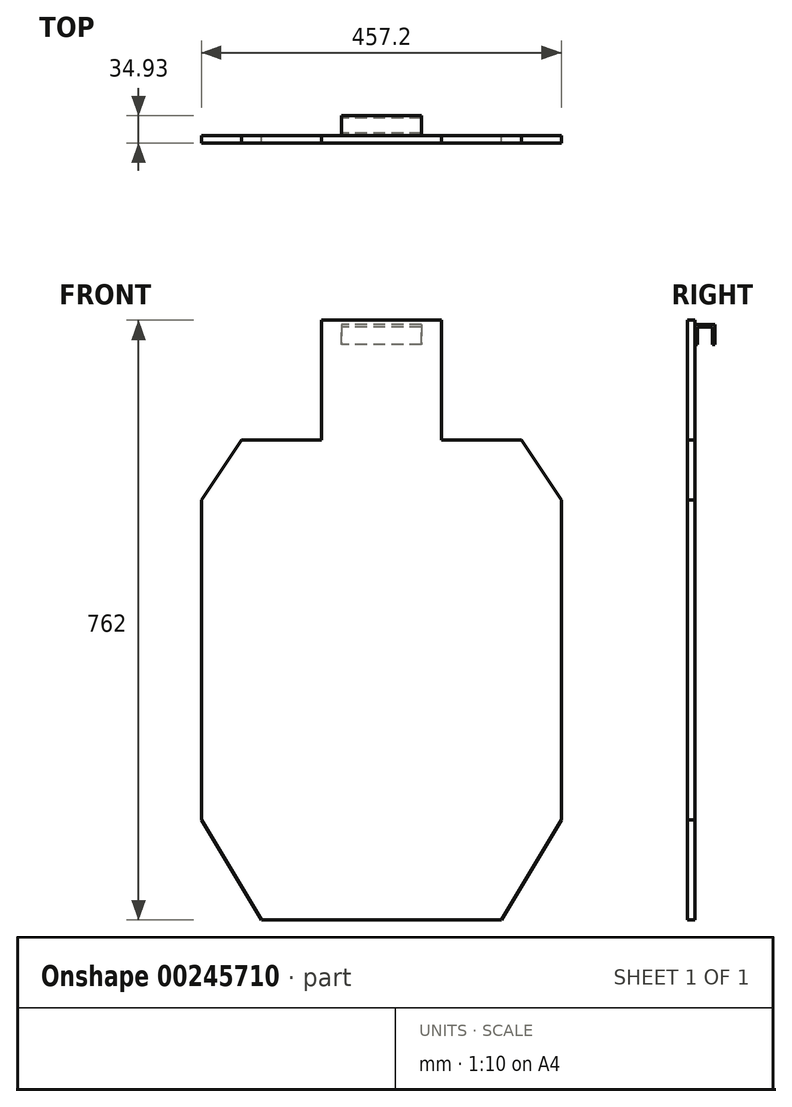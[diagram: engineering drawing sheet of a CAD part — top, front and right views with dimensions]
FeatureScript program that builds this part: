
annotation { "Feature Type Name" : "Feature", "Feature Type Description" : "" }
export const myFeature = defineFeature(function(context is Context, id is Id, definition is map)
    precondition{}
    {
        {
            var Q0;
            Q0=qCreatedBy(makeId("Front.planeOp"),FACE);
            var sketch = newSketch(context, id + "F0", { "sketchPlane" : qUnion([Q0])});
            skLineSegment(sketch, "E0.bottom", {"start": v(-177.8, 192.5) * mm, "end": v(177.8, 192.5) * mm});
            skLineSegment(sketch, "E0.top", {"start": v(-152.4, -417.1) * mm, "end": v(152.4, -417.1) * mm});
            skLineSegment(sketch, "E0.left", {"start": v(-228.6, 116.3) * mm, "end": v(-228.6, -290.1) * mm});
            skLineSegment(sketch, "E0.right", {"start": v(228.6, 116.3) * mm, "end": v(228.6, -290.1) * mm});
            skLineSegment(sketch, "E1.bottom", {"start": v(-76.2, 344.9) * mm, "end": v(76.2, 344.9) * mm});
            skLineSegment(sketch, "E1.top", {"start": v(-76.2, 192.5) * mm, "end": v(76.2, 192.5) * mm});
            skLineSegment(sketch, "E1.left", {"start": v(-76.2, 344.9) * mm, "end": v(-76.2, 192.5) * mm});
            skLineSegment(sketch, "E1.right", {"start": v(76.2, 344.9) * mm, "end": v(76.2, 192.5) * mm});
            skLineSegment(sketch, "E2", {"start": v(-228.6, 116.3) * mm, "end": v(-177.8, 192.5) * mm});
            skLineSegment(sketch, "E3", {"start": v(177.8, 192.5) * mm, "end": v(228.6, 116.3) * mm});
            skLineSegment(sketch, "E4", {"start": v(-228.6, -290.1) * mm, "end": v(-152.4, -417.1) * mm});
            skLineSegment(sketch, "E5", {"start": v(152.4, -417.1) * mm, "end": v(228.6, -290.1) * mm});
            skSolve(sketch);
        }
        {
            var Q0;
            Q0=makeQuery(id+"F0.imprint","IMPRINT",FACE,{"disambiguationData":[TD([[makeQuery(id+"F0.imprint","IMPRINT",EDGE,{"derivedFrom":sQuery(id+"F0.wireOp",EDGE,"E1.bottom")}),-1.0]])]});
            var Q1;
            Q1=makeQuery(id+"F0.imprint","IMPRINT",FACE,{"disambiguationData":[TD([[makeQuery(id+"F0.imprint","IMPRINT",EDGE,{"derivedFrom":sQuery(id+"F0.wireOp",EDGE,"E0.top")}),1.0]])]});
            extrude(context, id + "F1", {"entities" : qUnion([Q0, Q1]), "depth" : 9.52 * mm});
        }
        {
            var Q0;
            Q0=qCreatedBy(makeId("Right.planeOp"),FACE);
            var sketch = newSketch(context, id + "F2", { "sketchPlane" : qUnion([Q0])});
            skLineSegment(sketch, "E6", {"start": v(25.4, 314.14) * mm, "end": v(25.4, 339.54) * mm});
            skLineSegment(sketch, "E7", {"start": v(25.4, 339.54) * mm, "end": v(0, 339.54) * mm});
            skLineSegment(sketch, "E8", {"start": v(0, 339.54) * mm, "end": v(0, 314.14) * mm});
            skLineSegment(sketch, "E9", {"start": v(0, 314.14) * mm, "end": v(3.17, 314.14) * mm});
            skLineSegment(sketch, "E10", {"start": v(3.18, 314.14) * mm, "end": v(3.18, 336.36) * mm});
            skLineSegment(sketch, "E11", {"start": v(3.18, 336.36) * mm, "end": v(22.22, 336.36) * mm});
            skLineSegment(sketch, "E12", {"start": v(22.22, 336.36) * mm, "end": v(22.22, 314.14) * mm});
            skLineSegment(sketch, "E13", {"start": v(22.22, 314.14) * mm, "end": v(25.4, 314.14) * mm});
            skSolve(sketch);
        }
        {
            var Q0;
            Q0=makeQuery(id+"F2.imprint","IMPRINT",FACE,{"disambiguationData":[TD([[makeQuery(id+"F2.imprint","IMPRINT",EDGE,{"derivedFrom":sQuery(id+"F2.wireOp",EDGE,"E6")}),1.0]])]});
            extrude(context, id + "F3", {"entities" : qUnion([Q0]), "operationType" : NewBodyOperationType.ADD, "depth" : 50.8 * mm, "hasSecondDirection" : true, "secondDirectionOppositeDirection" : true, "secondDirectionDepth" : 50.8 * mm});
        }
    });
